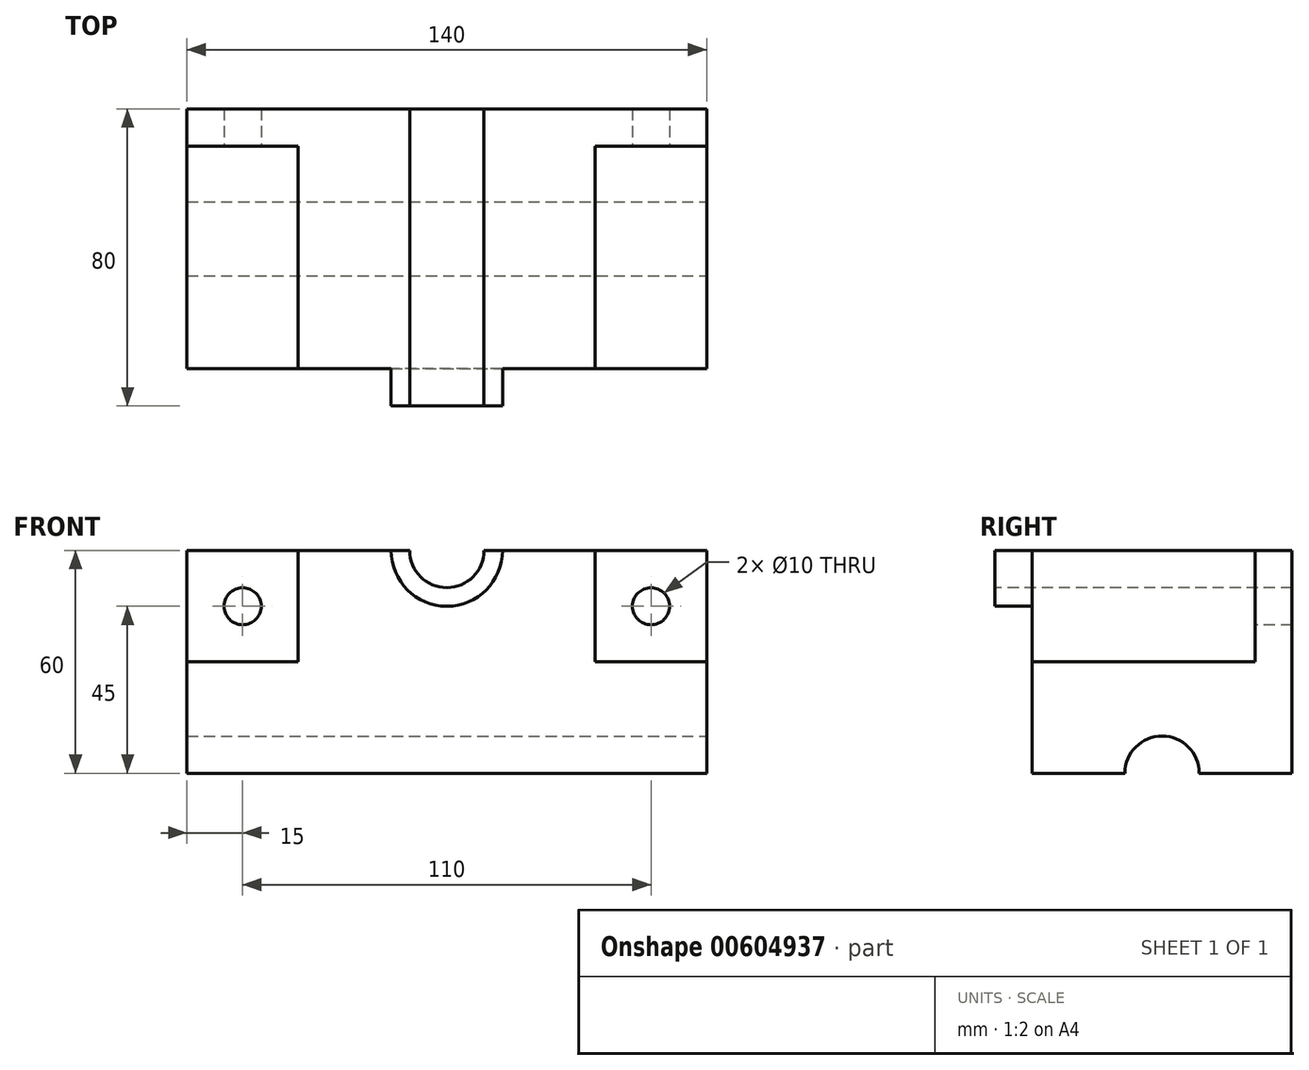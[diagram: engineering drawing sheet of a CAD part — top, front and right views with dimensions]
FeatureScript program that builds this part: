
annotation { "Feature Type Name" : "Feature", "Feature Type Description" : "" }
export const myFeature = defineFeature(function(context is Context, id is Id, definition is map)
    precondition{}
    {
        {
            var Q0;
            Q0=qCreatedBy(makeId("Front.planeOp"),FACE);
            var sketch = newSketch(context, id + "F0", { "sketchPlane" : qUnion([Q0])});
            skLineSegment(sketch, "E0.bottom", {"start": v(70, -60) * mm, "end": v(-70, -60) * mm});
            skLineSegment(sketch, "E0.top", {"start": v(70, 0) * mm, "end": v(10, 0) * mm});
            skLineSegment(sketch, "E0.left", {"start": v(70, -60) * mm, "end": v(70, 0) * mm});
            skLineSegment(sketch, "E0.right", {"start": v(-70, -60) * mm, "end": v(-70, 0) * mm});
            skPoint(sketch, "E0.middle", {"position": v(0, -30) * mm});
            skPoint(sketch, "E1.0", {"position": v(0, 0) * mm});
            skCircle(sketch, "E2", {"center": v(55, -15) * mm, "radius": 5 * mm});
            skCircle(sketch, "E3.MirrorC", {"center": v(-55, -15) * mm, "radius": 5 * mm});
            skLineSegment(sketch, "E4.trimOffspring", {"start": v(-10, 0) * mm, "end": v(-70, 0) * mm});
            skLineSegment(sketch, "E5", {"start": v(-10, 0) * mm, "end": v(10, 0) * mm});
            skSolve(sketch);
        }
        {
            var Q0;
            {var subQ0=sQuery(id+"F0.wireOp",EDGE,"TVRDKc7y-i53e-mgST-mGvM-R0ecqPcTSKbA");Q0=makeQuery(id+"F0.imprint","IMPRINT",FACE,{"disambiguationData":[TD([[makeQuery(id+"F0.imprint","IMPRINT",EDGE,{"derivedFrom":subQ0}),-1.0]])]});}
            var Q1;
            Q1=makeQuery(id+"F0.imprint","IMPRINT",FACE,{"disambiguationData":[TD([[makeQuery(id+"F0.imprint","IMPRINT",EDGE,{"derivedFrom":sQuery(id+"F0.wireOp",EDGE,"E0.bottom")}),-1.0]])]});
            extrude(context, id + "F1", {"entities" : qUnion([Q0, Q1]), "oppositeDirection" : true, "depth" : 70 * mm, "offsetDistance" : 25 * mm});
        }
        {
            var Q0;
            Q0=makeQuery(id+"F1.opExtrude","SWEPT_FACE",FACE,{"disambiguationData":[OSD([sQuery(id+"F0.wireOp",EDGE,"E0.left")])]});
            var sketch = newSketch(context, id + "F2", { "sketchPlane" : qUnion([Q0])});
            skCircle(sketch, "E6", {"center": v(35, -60) * mm, "radius": 10 * mm});
            skLineSegment(sketch, "E7", {"start": v(0, -30) * mm, "end": v(60, -30) * mm});
            skLineSegment(sketch, "E8", {"start": v(60, -30) * mm, "end": v(60, 0) * mm});
            skSolve(sketch);
        }
        {
            var Q0;
            {var subQ0=sQuery(id+"F2.wireOp",EDGE,"E6");var subQ1=makeQuery(id+"F1.opExtrude","SWEPT_EDGE",EDGE,{"disambiguationData":[OSD([sQuery(id+"F0.wireOp",EDGE,"E0.bottom"),sQuery(id+"F0.wireOp",EDGE,"E0.left")])]});var subQ2=makeQuery(id+"F2.imprint","INTERSECT",VERTEX,{"disambiguationData":[OD(0.0)],"derivedFrom":[subQ1,subQ0]});Q0=makeQuery(id+"F2.imprint","IMPRINT",FACE,{"disambiguationData":[TD([[makeQuery(id+"F2.imprint","IMPRINT",EDGE,{"disambiguationData":[TD([[subQ2,-1.0]])],"derivedFrom":subQ0}),1.0]])]});}
            var Q1;
            {var subQ0=sQuery(id+"F2.wireOp",EDGE,"E6");var subQ1=makeQuery(id+"F1.opExtrude","SWEPT_EDGE",EDGE,{"disambiguationData":[OSD([sQuery(id+"F0.wireOp",EDGE,"E0.bottom"),sQuery(id+"F0.wireOp",EDGE,"E0.left")])]});var subQ2=makeQuery(id+"F2.imprint","INTERSECT",VERTEX,{"disambiguationData":[OD(0.0)],"derivedFrom":[subQ1,subQ0]});Q1=makeQuery(id+"F2.imprint","IMPRINT",FACE,{"disambiguationData":[TD([[makeQuery(id+"F2.imprint","IMPRINT",EDGE,{"disambiguationData":[TD([[subQ2,1.0]])],"derivedFrom":subQ0}),1.0]])]});}
            extrude(context, id + "F3", {"entities" : qUnion([Q0, Q1]), "operationType" : NewBodyOperationType.REMOVE, "endBound" : BoundingType.THROUGH_ALL, "oppositeDirection" : true, "depth" : 25 * mm, "offsetDistance" : 25 * mm});
        }
        {
            var Q0;
            {var subQ0=sQuery(id+"F2.wireOp",EDGE,"E7");Q0=makeQuery(id+"F2.imprint","IMPRINT",FACE,{"disambiguationData":[TD([[makeQuery(id+"F2.imprint","IMPRINT",EDGE,{"derivedFrom":subQ0}),1.0]])]});}
            extrude(context, id + "F4", {"entities" : qUnion([Q0]), "operationType" : NewBodyOperationType.REMOVE, "oppositeDirection" : true, "depth" : 30 * mm, "offsetDistance" : 25 * mm});
        }
        {
            var Q0;
            Q0=makeQuery(id+"F1.opExtrude","CAP_FACE",FACE,{"disambiguationData":[OSD([sQuery(id+"F0.wireOp",EDGE,"E0.bottom"),sQuery(id+"F0.wireOp",EDGE,"E0.top"),sQuery(id+"F0.wireOp",EDGE,"E0.left"),sQuery(id+"F0.wireOp",EDGE,"E0.right"),sQuery(id+"F0.wireOp",EDGE,"TVRDKc7y-i53e-mgST-mGvM-R0ecqPcTSKbA"),sQuery(id+"F0.wireOp",EDGE,"E2"),sQuery(id+"F0.wireOp",EDGE,"E3.MirrorC"),sQuery(id+"F0.wireOp",EDGE,"E4.trimOffspring")])],"isStart":true});
            var sketch = newSketch(context, id + "F5", { "sketchPlane" : qUnion([Q0])});
            skLineSegment(sketch, "E9", {"start": v(-40, -30) * mm, "end": v(-70, -30) * mm});
            skLineSegment(sketch, "E10", {"start": v(-40, -30) * mm, "end": v(-40, 0) * mm});
            skSolve(sketch);
        }
        {
            var Q0;
            Q0 = qSketchRegion(id + "F5", true);
            var Q1;
            {var subQ4=sQuery(id+"F5.wireOp",EDGE,"E9");Q1=makeQuery(id+"F5.imprint","IMPRINT",FACE,{"disambiguationData":[TD([[makeQuery(id+"F5.imprint","IMPRINT",EDGE,{"derivedFrom":subQ4}),-1.0]])]});}
            extrude(context, id + "F6", {"entities" : qUnion([Q0, Q1]), "operationType" : NewBodyOperationType.REMOVE, "oppositeDirection" : true, "depth" : 60 * mm, "offsetDistance" : 25 * mm});
        }
        {
            var Q0;
            Q0=makeQuery(id+"F1.opExtrude","CAP_FACE",FACE,{"disambiguationData":[OSD([sQuery(id+"F0.wireOp",EDGE,"E0.bottom"),sQuery(id+"F0.wireOp",EDGE,"E0.top"),sQuery(id+"F0.wireOp",EDGE,"E0.left"),sQuery(id+"F0.wireOp",EDGE,"E0.right"),sQuery(id+"F0.wireOp",EDGE,"E2"),sQuery(id+"F0.wireOp",EDGE,"E3.MirrorC"),sQuery(id+"F0.wireOp",EDGE,"E4.trimOffspring"),sQuery(id+"F0.wireOp",EDGE,"E5")])],"isStart":true});
            var sketch = newSketch(context, id + "F7", { "sketchPlane" : qUnion([Q0])});
            skCircle(sketch, "E11", {"center": v(0, 0) * mm, "radius": 10 * mm});
            skCircle(sketch, "E12", {"center": v(0, 0) * mm, "radius": 15 * mm});
            skSolve(sketch);
        }
        {
            var Q0;
            {var subQ0=sQuery(id+"F7.wireOp",EDGE,"E11");var subQ1=makeQuery(id+"F1.opExtrude","CAP_EDGE",EDGE,{"disambiguationData":[OSD([sQuery(id+"F0.wireOp",EDGE,"E0.top"),sQuery(id+"F0.wireOp",EDGE,"E4.trimOffspring"),sQuery(id+"F0.wireOp",EDGE,"E5")])],"isStart":true});var subQ2=makeQuery(id+"F7.imprint","INTERSECT",VERTEX,{"disambiguationData":[OD(0.0)],"derivedFrom":[subQ1,subQ0]});Q0=makeQuery(id+"F7.imprint","IMPRINT",FACE,{"disambiguationData":[TD([[makeQuery(id+"F7.imprint","IMPRINT",EDGE,{"disambiguationData":[TD([[subQ2,1.0]])],"derivedFrom":subQ0}),1.0]])]});}
            extrude(context, id + "F8", {"entities" : qUnion([Q0]), "operationType" : NewBodyOperationType.REMOVE, "endBound" : BoundingType.THROUGH_ALL, "oppositeDirection" : true, "depth" : 25 * mm, "offsetDistance" : 25 * mm});
        }
        {
            var Q0;
            {var subQ0=sQuery(id+"F7.wireOp",EDGE,"E11");var subQ1=makeQuery(id+"F1.opExtrude","CAP_EDGE",EDGE,{"disambiguationData":[OSD([sQuery(id+"F0.wireOp",EDGE,"E0.top"),sQuery(id+"F0.wireOp",EDGE,"E4.trimOffspring"),sQuery(id+"F0.wireOp",EDGE,"E5")])],"isStart":true});var subQ2=makeQuery(id+"F7.imprint","INTERSECT",VERTEX,{"disambiguationData":[OD(0.0)],"derivedFrom":[subQ1,subQ0]});Q0=makeQuery(id+"F7.imprint","IMPRINT",FACE,{"disambiguationData":[TD([[makeQuery(id+"F7.imprint","IMPRINT",EDGE,{"disambiguationData":[TD([[subQ2,1.0]])],"derivedFrom":subQ0}),-1.0]])]});}
            extrude(context, id + "F9", {"entities" : qUnion([Q0]), "operationType" : NewBodyOperationType.ADD, "depth" : 10 * mm, "offsetDistance" : 25 * mm});
        }
    });
